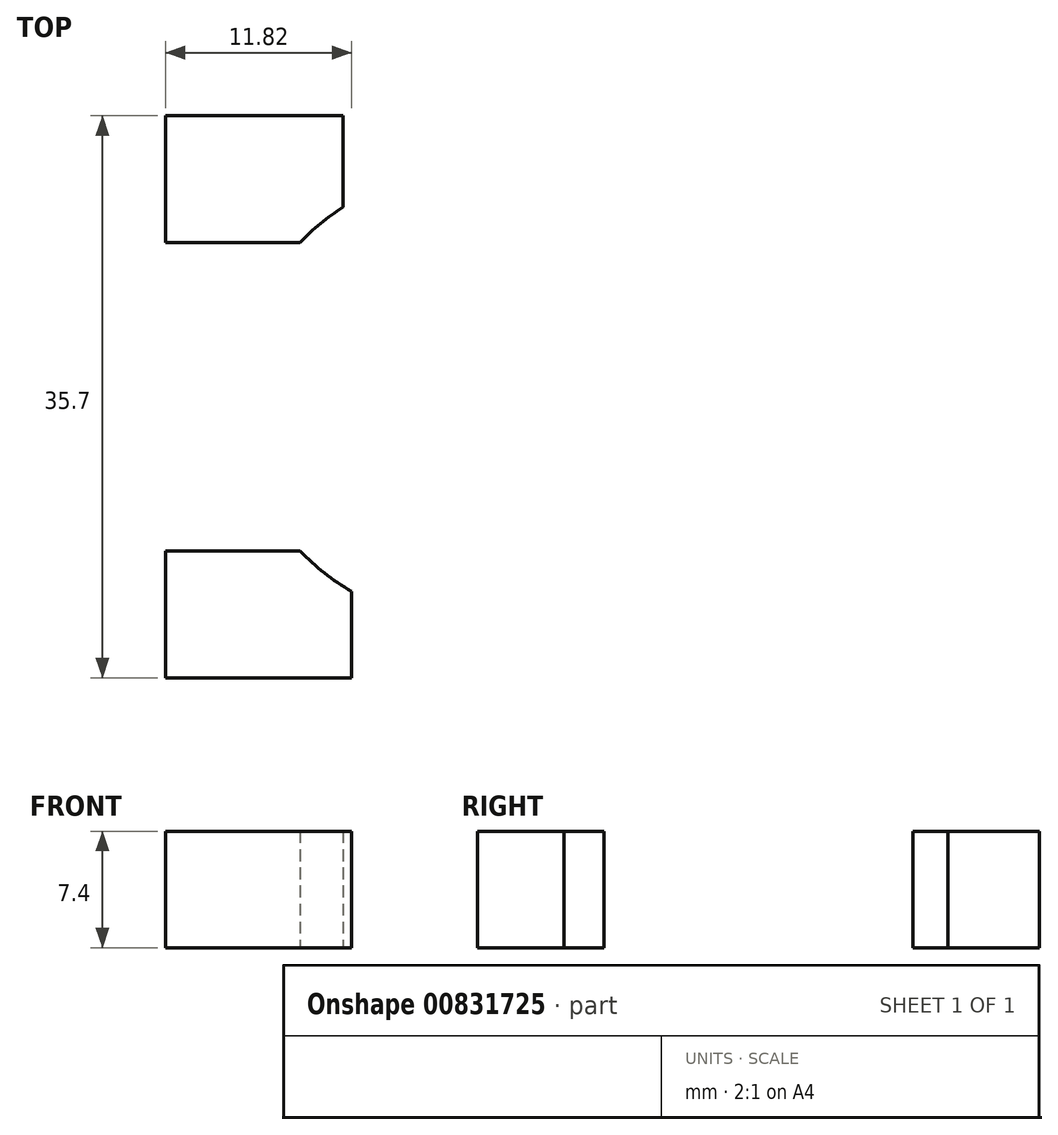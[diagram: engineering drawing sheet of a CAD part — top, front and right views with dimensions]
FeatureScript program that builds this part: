
annotation { "Feature Type Name" : "Feature", "Feature Type Description" : "" }
export const myFeature = defineFeature(function(context is Context, id is Id, definition is map)
    precondition{}
    {
        {
            var Q0;
            Q0=qCreatedBy(makeId("Top.planeOp"),FACE);
            var sketch = newSketch(context, id + "F0", { "sketchPlane" : qUnion([Q0])});
            skCircle(sketch, "E0", {"center": v(0, 0) * mm, "radius": 14.26 * mm});
            skLineSegment(sketch, "E1.bottom", {"start": v(-18.93, 17.85) * mm, "end": v(-7.65, 17.85) * mm});
            skLineSegment(sketch, "E1.top", {"start": v(-18.93, -17.85) * mm, "end": v(-7.11, -17.85) * mm});
            skLineSegment(sketch, "E1.left", {"start": v(-18.93, 17.85) * mm, "end": v(-18.93, 9.8) * mm});
            skLineSegment(sketch, "E1.right", {"start": v(18.93, 17.85) * mm, "end": v(18.93, 9.8) * mm});
            skLineSegment(sketch, "E2.bottom", {"start": v(-18.93, 9.8) * mm, "end": v(-7.65, 9.8) * mm});
            skLineSegment(sketch, "E2.left", {"start": v(-18.93, 9.8) * mm, "end": v(-18.93, 17.85) * mm});
            skLineSegment(sketch, "E2.right", {"start": v(-7.65, 9.8) * mm, "end": v(-7.65, 17.85) * mm});
            skLineSegment(sketch, "E3.1.0", {"start": v(7.65, -9.8) * mm, "end": v(7.65, -17.85) * mm});
            skLineSegment(sketch, "E3.1.1", {"start": v(18.93, -9.8) * mm, "end": v(7.65, -9.8) * mm});
            skLineSegment(sketch, "E3.1.2", {"start": v(18.93, -9.8) * mm, "end": v(18.93, -17.85) * mm});
            skLineSegment(sketch, "E3.1.3", {"start": v(18.93, -17.85) * mm, "end": v(7.65, -17.85) * mm});
            skLineSegment(sketch, "E3.1.4", {"start": v(18.93, -17.85) * mm, "end": v(18.93, -9.8) * mm});
            skLineSegment(sketch, "E3.1.5", {"start": v(18.93, -17.85) * mm, "end": v(7.65, -17.85) * mm});
            skLineSegment(sketch, "E3.anchor1", {"start": v(0, 0) * mm, "end": v(-7.65, 9.8) * mm, "construction": true});
            skLineSegment(sketch, "E3.anchor2", {"start": v(0, 0) * mm, "end": v(7.65, -9.8) * mm, "construction": true});
            skLineSegment(sketch, "E4.bottom", {"start": v(-18.93, -9.8) * mm, "end": v(-7.11, -9.8) * mm});
            skLineSegment(sketch, "E4.left", {"start": v(-18.93, -9.8) * mm, "end": v(-18.93, -17.85) * mm});
            skLineSegment(sketch, "E4.right", {"start": v(-7.11, -9.8) * mm, "end": v(-7.11, -17.85) * mm});
            skLineSegment(sketch, "E5.1.0", {"start": v(18.93, 9.8) * mm, "end": v(7.11, 9.8) * mm});
            skLineSegment(sketch, "E5.1.1", {"start": v(7.11, 9.8) * mm, "end": v(7.11, 17.85) * mm});
            skLineSegment(sketch, "E5.1.2", {"start": v(18.93, 17.85) * mm, "end": v(7.11, 17.85) * mm});
            skLineSegment(sketch, "E5.1.3", {"start": v(18.93, 9.8) * mm, "end": v(18.93, 17.85) * mm});
            skLineSegment(sketch, "E6.trimOffspring", {"start": v(7.11, 17.85) * mm, "end": v(18.93, 17.85) * mm});
            skLineSegment(sketch, "E7.trimOffspring", {"start": v(-7.11, -17.85) * mm, "end": v(-18.93, -17.85) * mm});
            skLineSegment(sketch, "E8.trimOffspring", {"start": v(7.65, -17.85) * mm, "end": v(18.93, -17.85) * mm});
            skSolve(sketch);
        }
        {
            var Q0;
            {var subQ1=sQuery(id+"F0.wireOp",EDGE,"E1.bottom");Q0=makeQuery(id+"F0.imprint","IMPRINT",FACE,{"disambiguationData":[TD([[makeQuery(id+"F0.imprint","IMPRINT",EDGE,{"derivedFrom":subQ1}),-1.0]])]});}
            var Q1;
            {var subQ0=sQuery(id+"F0.wireOp",EDGE,"E6.trimOffspring");Q1=makeQuery(id+"F0.imprint","IMPRINT",FACE,{"disambiguationData":[TD([[makeQuery(id+"F0.imprint","IMPRINT",EDGE,{"derivedFrom":subQ0}),-1.0]])]});}
            var Q2;
            {var subQ0=sQuery(id+"F0.wireOp",EDGE,"E3.1.2");Q2=makeQuery(id+"F0.imprint","IMPRINT",FACE,{"disambiguationData":[TD([[makeQuery(id+"F0.imprint","IMPRINT",EDGE,{"derivedFrom":subQ0}),-1.0]])]});}
            var Q3;
            {var subQ0=sQuery(id+"F0.wireOp",EDGE,"E4.left");Q3=makeQuery(id+"F0.imprint","IMPRINT",FACE,{"disambiguationData":[TD([[makeQuery(id+"F0.imprint","IMPRINT",EDGE,{"derivedFrom":subQ0}),1.0]])]});}
            extrude(context, id + "F1", {"entities" : qUnion([Q0, Q1, Q2, Q3]), "depth" : 7.4 * mm, "offsetDistance" : 25.4 * mm});
        }
    });
